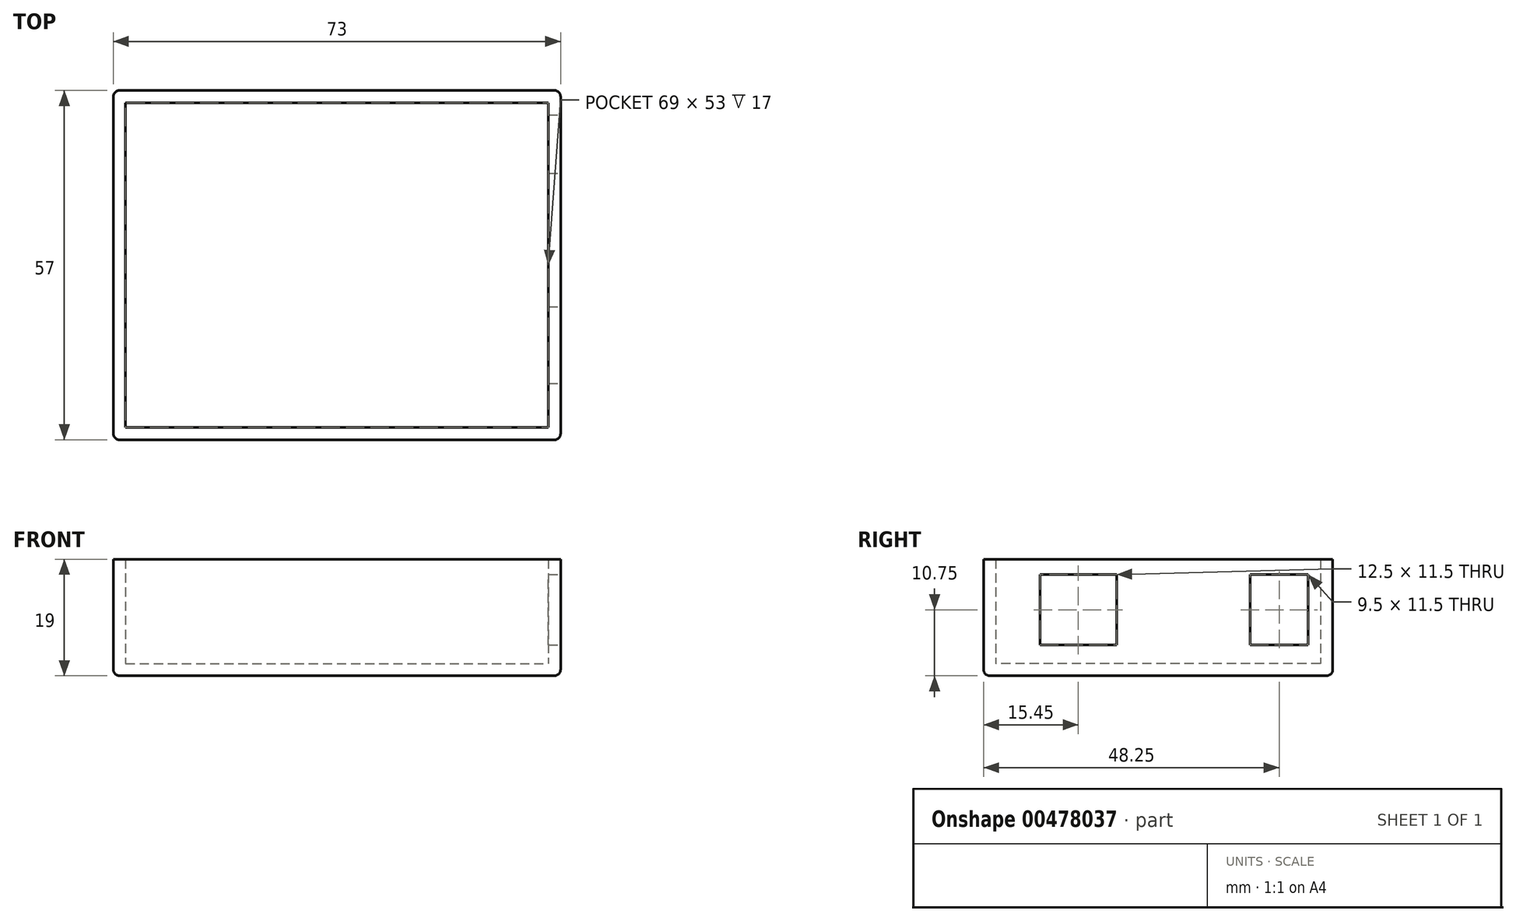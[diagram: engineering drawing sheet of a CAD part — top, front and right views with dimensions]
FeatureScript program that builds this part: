
annotation { "Feature Type Name" : "Feature", "Feature Type Description" : "" }
export const myFeature = defineFeature(function(context is Context, id is Id, definition is map)
    precondition{}
    {
        {
            var Q0;
            Q0=qCreatedBy(makeId("Top.planeOp"),FACE);
            var sketch = newSketch(context, id + "F0", { "sketchPlane" : qUnion([Q0])});
            skLineSegment(sketch, "E0.bottom", {"start": v(-36.5, 28.5) * mm, "end": v(36.5, 28.5) * mm});
            skLineSegment(sketch, "E0.top", {"start": v(-36.5, -28.5) * mm, "end": v(36.5, -28.5) * mm});
            skLineSegment(sketch, "E0.left", {"start": v(-36.5, 28.5) * mm, "end": v(-36.5, -28.5) * mm});
            skLineSegment(sketch, "E0.right", {"start": v(36.5, 28.5) * mm, "end": v(36.5, -28.5) * mm});
            skPoint(sketch, "E0.middle", {"position": v(0, 0) * mm});
            skSolve(sketch);
        }
        {
            var Q0;
            Q0=makeQuery(id+"F0.imprint","IMPRINT",FACE,{"disambiguationData":[TD([[makeQuery(id+"F0.imprint","IMPRINT",EDGE,{"derivedFrom":sQuery(id+"F0.wireOp",EDGE,"E0.bottom")}),-1.0]])]});
            extrude(context, id + "F1", {"entities" : qUnion([Q0]), "depth" : 19 * mm});
        }
        {
            var Q0;
            Q0=makeQuery(id+"F1.opExtrude","CAP_FACE",FACE,{"disambiguationData":[OSD([sQuery(id+"F0.wireOp",EDGE,"E0.bottom"),sQuery(id+"F0.wireOp",EDGE,"E0.top"),sQuery(id+"F0.wireOp",EDGE,"E0.left"),sQuery(id+"F0.wireOp",EDGE,"E0.right")])],"isStart":false});
            shell(context, id + "F2", {"entities" : qUnion([Q0]), "thickness" : 2 * mm});
        }
        {
            var Q0;
            Q0=makeQuery(id+"F1.opExtrude","SWEPT_FACE",FACE,{"disambiguationData":[OSD([sQuery(id+"F0.wireOp",EDGE,"E0.right")])]});
            var sketch = newSketch(context, id + "F3", { "sketchPlane" : qUnion([Q0])});
            skLineSegment(sketch, "E1.bottom", {"start": v(-6.8, 5) * mm, "end": v(-19.3, 5) * mm});
            skLineSegment(sketch, "E1.top", {"start": v(-6.8, 16.5) * mm, "end": v(-19.3, 16.5) * mm});
            skLineSegment(sketch, "E1.left", {"start": v(-6.8, 5) * mm, "end": v(-6.8, 16.5) * mm});
            skLineSegment(sketch, "E1.right", {"start": v(-19.3, 5) * mm, "end": v(-19.3, 16.5) * mm});
            skPoint(sketch, "E1.middle", {"position": v(-13.05, 10.75) * mm});
            skSolve(sketch);
        }
        {
            var Q0;
            {var subQ0=sQuery(id+"F0.wireOp",EDGE,"E0.right");var subQ1=makeQuery(id+"F1.opExtrude","CAP_EDGE",EDGE,{"disambiguationData":[OSD([subQ0])],"isStart":true});Q0=makeQuery(id+"F3.imprint","IMPRINT",FACE,{"disambiguationData":[TD([[makeQuery(id+"F3.imprint","IMPRINT",EDGE,{"derivedFrom":subQ1}),-1.0]])]});}
            var sketch = newSketch(context, id + "F4", { "sketchPlane" : qUnion([Q0])});
            skLineSegment(sketch, "E2.bottom", {"start": v(24.5, 5) * mm, "end": v(15, 5) * mm});
            skLineSegment(sketch, "E2.top", {"start": v(24.5, 16.5) * mm, "end": v(15, 16.5) * mm});
            skLineSegment(sketch, "E2.left", {"start": v(24.5, 5) * mm, "end": v(24.5, 16.5) * mm});
            skLineSegment(sketch, "E2.right", {"start": v(15, 5) * mm, "end": v(15, 16.5) * mm});
            skPoint(sketch, "E2.middle", {"position": v(19.75, 10.75) * mm});
            skSolve(sketch);
        }
        {
            var Q0;
            Q0 = qSketchRegion(id + "F3", true);
            extrude(context, id + "F5", {"entities" : qUnion([Q0]), "operationType" : NewBodyOperationType.REMOVE, "oppositeDirection" : true, "depth" : 25 * mm});
        }
        {
            var Q0;
            Q0 = qSketchRegion(id + "F4", true);
            extrude(context, id + "F6", {"entities" : qUnion([Q0]), "operationType" : NewBodyOperationType.REMOVE, "oppositeDirection" : true, "depth" : 25 * mm});
        }
        {
            var Q0;
            Q0=makeQuery(id+"F1.opExtrude","CAP_EDGE",EDGE,{"disambiguationData":[OSD([sQuery(id+"F0.wireOp",EDGE,"E0.top")])],"isStart":true});
            var Q1;
            Q1=makeQuery(id+"F1.opExtrude","CAP_EDGE",EDGE,{"disambiguationData":[OSD([sQuery(id+"F0.wireOp",EDGE,"E0.bottom")])],"isStart":true});
            var Q2;
            Q2=makeQuery(id+"F1.opExtrude","CAP_EDGE",EDGE,{"disambiguationData":[OSD([sQuery(id+"F0.wireOp",EDGE,"E0.left")])],"isStart":true});
            var Q3;
            Q3=makeQuery(id+"F1.opExtrude","SWEPT_EDGE",EDGE,{"disambiguationData":[OSD([sQuery(id+"F0.wireOp",EDGE,"E0.top"),sQuery(id+"F0.wireOp",EDGE,"E0.right")])]});
            var Q4;
            Q4=makeQuery(id+"F1.opExtrude","CAP_EDGE",EDGE,{"disambiguationData":[OSD([sQuery(id+"F0.wireOp",EDGE,"E0.right")])],"isStart":true});
            var Q5;
            Q5=makeQuery(id+"F1.opExtrude","SWEPT_EDGE",EDGE,{"disambiguationData":[OSD([sQuery(id+"F0.wireOp",EDGE,"E0.top"),sQuery(id+"F0.wireOp",EDGE,"E0.left")])]});
            var Q6;
            Q6=makeQuery(id+"F1.opExtrude","SWEPT_EDGE",EDGE,{"disambiguationData":[OSD([sQuery(id+"F0.wireOp",EDGE,"E0.bottom"),sQuery(id+"F0.wireOp",EDGE,"E0.right")])]});
            var Q7;
            Q7=makeQuery(id+"F1.opExtrude","SWEPT_EDGE",EDGE,{"disambiguationData":[OSD([sQuery(id+"F0.wireOp",EDGE,"E0.bottom"),sQuery(id+"F0.wireOp",EDGE,"E0.left")])]});
            fillet(context, id + "F7", {"entities" : qUnion([Q0, Q1, Q2, Q3, Q4, Q5, Q6, Q7]), "radius" : 1 * mm, "tangentPropagation" : true, "allowEdgeOverflow" : false});
        }
    });
